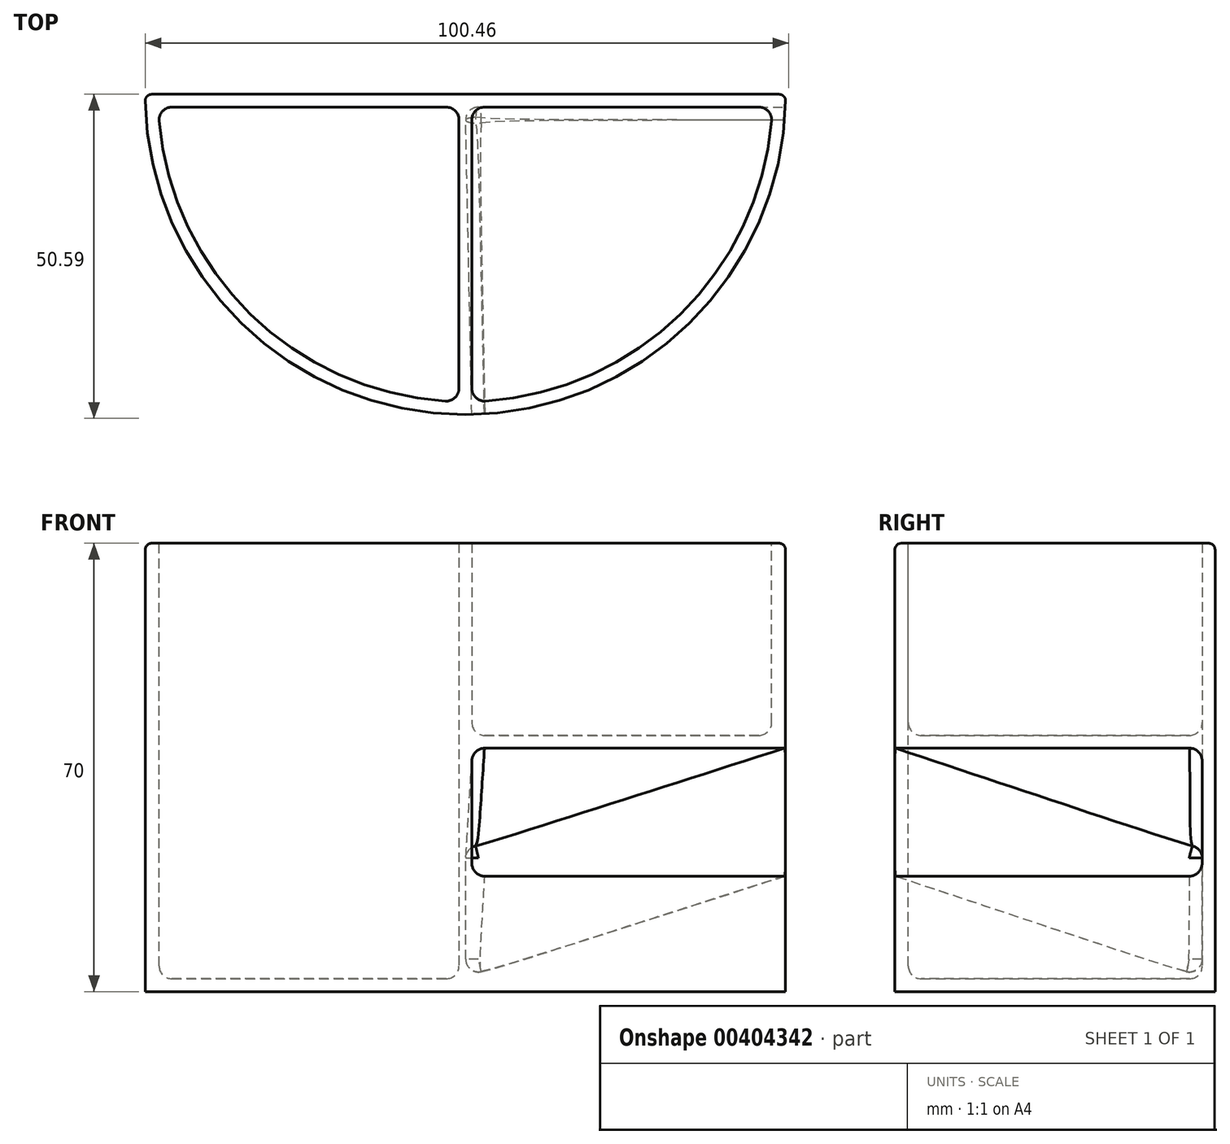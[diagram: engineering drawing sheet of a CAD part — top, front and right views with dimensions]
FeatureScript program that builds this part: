
annotation { "Feature Type Name" : "Feature", "Feature Type Description" : "" }
export const myFeature = defineFeature(function(context is Context, id is Id, definition is map)
    precondition{}
    {
        {
            var Q0;
            Q0=qCreatedBy(makeId("Top.planeOp"),FACE);
            var sketch = newSketch(context, id + "F0", { "sketchPlane" : qUnion([Q0])});
            skArc(sketch, "E0", {"start": v(-50, 0) * mm, "mid": v(0, -50) * mm, "end": v(50, 0) * mm});
            skLineSegment(sketch, "E1", {"start": v(-50, 0) * mm, "end": v(50, 0) * mm});
            skSolve(sketch);
        }
        {
            var Q0;
            Q0 = qSketchRegion(id + "F0", true);
            extrude(context, id + "F1", {"entities" : qUnion([Q0]), "depth" : 70 * mm});
        }
        {
            var Q0;
            Q0=makeQuery(id+"F1.opExtrude","CAP_FACE",FACE,{"disambiguationData":[OSD([sQuery(id+"F0.wireOp",EDGE,"E0"),sQuery(id+"F0.wireOp",EDGE,"E1")])],"isStart":false});
            cPlane(context, id + "F2", {"entities" : qUnion([Q0]), "cplaneType" : CPlaneType.OFFSET, "offset" : 32 * mm, "oppositeDirection" : true, "width" : 150 * mm, "height" : 150 * mm});
        }
        {
            var Q0;
            Q0=qCreatedBy(id+"F2.planeOp",FACE);
            cPlane(context, id + "F3", {"entities" : qUnion([Q0]), "cplaneType" : CPlaneType.OFFSET, "offset" : 20 * mm, "oppositeDirection" : true, "width" : 150 * mm, "height" : 150 * mm});
        }
        {
            var Q0;
            Q0=qCreatedBy(id+"F2.planeOp",FACE);
            var sketch = newSketch(context, id + "F4", { "sketchPlane" : qUnion([Q0])});
            skArc(sketch, "E2", {"start": v(1, -49.99) * mm, "mid": v(35, -35.7) * mm, "end": v(49.96, -2) * mm});
            skSolve(sketch);
        }
        {
            var Q0;
            Q0=qCreatedBy(id+"F3.planeOp",FACE);
            var sketch = newSketch(context, id + "F5", { "sketchPlane" : qUnion([Q0])});
            skArc(sketch, "E3", {"start": v(1, -49.99) * mm, "mid": v(35, -35.7) * mm, "end": v(49.96, -2) * mm});
            skSolve(sketch);
        }
        {
            var Q0;
            Q0=qCreatedBy(makeId("Front.planeOp"),FACE);
            cPlane(context, id + "F6", {"entities" : qUnion([Q0]), "cplaneType" : CPlaneType.OFFSET, "offset" : 2 * mm, "width" : 150 * mm, "height" : 150 * mm});
        }
        {
            var Q0;
            Q0=qCreatedBy(id+"F6.planeOp",FACE);
            var sketch = newSketch(context, id + "F7", { "sketchPlane" : qUnion([Q0])});
            skLineSegment(sketch, "E4", {"start": v(0, 2) * mm, "end": v(0, 22) * mm});
            skSolve(sketch);
        }
        {
            var Q0;
            Q0=sQuery(id+"F7.wireOp",VERTEX,"E4.end");
            var Q1;
            Q1=sQuery(id+"F4.wireOp",EDGE,"E2");
            var Q2;
            Q2=sQuery(id+"F7.wireOp",VERTEX,"E4.end");
            loft(context, id + "F8", {"bodyType" : ToolBodyType.SURFACE, "sheetProfilesArray" : [{ "sheetProfileEntities" : qUnion([Q0]) }], "wireProfilesArray" : [{ "wireProfileEntities" : qUnion([Q1]) }, { "wireProfileEntities" : qUnion([Q2]) }]});
        }
        {
            var Q0;
            Q0=sQuery(id+"F5.wireOp",EDGE,"E3");
            var Q1;
            Q1=sQuery(id+"F7.wireOp",VERTEX,"E4.start");
            loft(context, id + "F9", {"bodyType" : ToolBodyType.SURFACE, "wireProfilesArray" : [{ "wireProfileEntities" : qUnion([Q0]) }, { "wireProfileEntities" : qUnion([Q1]) }]});
        }
        {
            var Q1;
            Q1=makeQuery(id+"F8.opLoft","SWEPT_FACE",FACE,{"disambiguationData":[OSD([sQuery(id+"F4.wireOp",VERTEX,"E2.start"),sQuery(id+"F4.wireOp",VERTEX,"E2.end"),sQuery(id+"F4.wireOp",EDGE,"E2")])]});
            var Q2;
            Q2=makeQuery(id+"F9.opLoft","SWEPT_FACE",FACE,{"disambiguationData":[OSD([sQuery(id+"F5.wireOp",VERTEX,"E3.start"),sQuery(id+"F5.wireOp",VERTEX,"E3.end"),sQuery(id+"F5.wireOp",EDGE,"E3")])]});
            loft(context, id + "F10", {"operationType" : NewBodyOperationType.REMOVE, "sheetProfilesArray" : [{ "sheetProfileEntities" : qUnion([Q1]) }, { "sheetProfileEntities" : qUnion([Q2]) }]});
        }
        {
            var Q0;
            Q0=makeQuery(id+"F1.opExtrude","CAP_FACE",FACE,{"disambiguationData":[OSD([sQuery(id+"F0.wireOp",EDGE,"E0"),sQuery(id+"F0.wireOp",EDGE,"E1")])],"isStart":false});
            var sketch = newSketch(context, id + "F11", { "sketchPlane" : qUnion([Q0])});
            skArc(sketch, "E5", {"start": v(47.96, -2) * mm, "mid": v(33.59, -34.3) * mm, "end": v(1, -47.99) * mm});
            skLineSegment(sketch, "E6", {"start": v(47.96, -2) * mm, "end": v(1, -2) * mm});
            skLineSegment(sketch, "E7", {"start": v(1, -2) * mm, "end": v(1, -47.99) * mm});
            skSolve(sketch);
        }
        {
            var Q0;
            Q0=makeQuery(id+"F11.imprint","IMPRINT",FACE,{"disambiguationData":[TD([[makeQuery(id+"F11.imprint","IMPRINT",EDGE,{"derivedFrom":sQuery(id+"F11.wireOp",EDGE,"E5")}),1.0]])]});
            var sketch = newSketch(context, id + "F12", { "sketchPlane" : qUnion([Q0])});
            skArc(sketch, "E8", {"start": v(-47.96, -2) * mm, "mid": v(-33.59, -34.3) * mm, "end": v(-1, -47.99) * mm});
            skLineSegment(sketch, "E9", {"start": v(-1, -47.99) * mm, "end": v(-1, -2) * mm});
            skLineSegment(sketch, "E10", {"start": v(-1, -2) * mm, "end": v(-47.96, -2) * mm});
            skSolve(sketch);
        }
        {
            var Q0;
            Q0 = qSketchRegion(id + "F11", true);
            extrude(context, id + "F13", {"entities" : qUnion([Q0]), "operationType" : NewBodyOperationType.REMOVE, "oppositeDirection" : true, "depth" : 30 * mm});
        }
        {
            var Q0;
            Q0 = qSketchRegion(id + "F12", true);
            extrude(context, id + "F14", {"entities" : qUnion([Q0]), "operationType" : NewBodyOperationType.REMOVE, "oppositeDirection" : true, "depth" : 68 * mm});
        }
        {
            var Q0;
            Q0=makeQuery(id+"F14.boolean.opBoolean","COPY",EDGE,{"derivedFrom":makeQuery(id+"F14.opExtrude","CAP_EDGE",EDGE,{"disambiguationData":[OSD([sQuery(id+"F12.wireOp",EDGE,"E10")])],"isStart":false})});
            var Q1;
            Q1=makeQuery(id+"F14.boolean.opBoolean","COPY",EDGE,{"derivedFrom":makeQuery(id+"F14.opExtrude","CAP_EDGE",EDGE,{"disambiguationData":[OSD([sQuery(id+"F12.wireOp",EDGE,"E9")])],"isStart":false})});
            var Q2;
            Q2=makeQuery(id+"F14.boolean.opBoolean","COPY",EDGE,{"derivedFrom":makeQuery(id+"F14.opExtrude","SWEPT_EDGE",EDGE,{"disambiguationData":[OSD([sQuery(id+"F12.wireOp",EDGE,"E9"),sQuery(id+"F12.wireOp",EDGE,"E10")])]})});
            var Q3;
            Q3=makeQuery(id+"F14.boolean.opBoolean","COPY",EDGE,{"derivedFrom":makeQuery(id+"F14.opExtrude","SWEPT_EDGE",EDGE,{"disambiguationData":[OSD([sQuery(id+"F12.wireOp",EDGE,"E8"),sQuery(id+"F12.wireOp",EDGE,"E9")])]})});
            var Q4;
            Q4=makeQuery(id+"F14.boolean.opBoolean","COPY",EDGE,{"derivedFrom":makeQuery(id+"F14.opExtrude","CAP_EDGE",EDGE,{"disambiguationData":[OSD([sQuery(id+"F12.wireOp",EDGE,"E8")])],"isStart":false})});
            var Q5;
            Q5=makeQuery(id+"F14.boolean.opBoolean","COPY",EDGE,{"derivedFrom":makeQuery(id+"F14.opExtrude","SWEPT_EDGE",EDGE,{"disambiguationData":[OSD([sQuery(id+"F12.wireOp",EDGE,"E8"),sQuery(id+"F12.wireOp",EDGE,"E10")])]})});
            var Q6;
            Q6=makeQuery(id+"F13.boolean.opBoolean","COPY",EDGE,{"derivedFrom":makeQuery(id+"F13.opExtrude","SWEPT_EDGE",EDGE,{"disambiguationData":[OSD([sQuery(id+"F11.wireOp",EDGE,"E6"),sQuery(id+"F11.wireOp",EDGE,"E7")])]})});
            var Q7;
            Q7=makeQuery(id+"F13.boolean.opBoolean","COPY",EDGE,{"derivedFrom":makeQuery(id+"F13.opExtrude","SWEPT_EDGE",EDGE,{"disambiguationData":[OSD([sQuery(id+"F11.wireOp",EDGE,"E5"),sQuery(id+"F11.wireOp",EDGE,"E6")])]})});
            var Q8;
            Q8=makeQuery(id+"F13.boolean.opBoolean","COPY",EDGE,{"derivedFrom":makeQuery(id+"F13.opExtrude","CAP_EDGE",EDGE,{"disambiguationData":[OSD([sQuery(id+"F11.wireOp",EDGE,"E5")])],"isStart":false})});
            var Q9;
            Q9=makeQuery(id+"F13.boolean.opBoolean","COPY",EDGE,{"derivedFrom":makeQuery(id+"F13.opExtrude","CAP_EDGE",EDGE,{"disambiguationData":[OSD([sQuery(id+"F11.wireOp",EDGE,"E6")])],"isStart":false})});
            var Q10;
            Q10=makeQuery(id+"F13.boolean.opBoolean","COPY",EDGE,{"derivedFrom":makeQuery(id+"F13.opExtrude","CAP_EDGE",EDGE,{"disambiguationData":[OSD([sQuery(id+"F11.wireOp",EDGE,"E7")])],"isStart":false})});
            var Q11;
            Q11=makeQuery(id+"F13.boolean.opBoolean","COPY",EDGE,{"derivedFrom":makeQuery(id+"F13.opExtrude","SWEPT_EDGE",EDGE,{"disambiguationData":[OSD([sQuery(id+"F11.wireOp",EDGE,"E5"),sQuery(id+"F11.wireOp",EDGE,"E7")])]})});
            var Q12;
            Q12=makeQuery(id+"F10.boolean.opBoolean","COPY",EDGE,{"derivedFrom":makeQuery(id+"F10.opLoft","MID_CAP_EDGE",EDGE,{"disambiguationData":[OSD([sQuery(id+"F4.wireOp",VERTEX,"E2.end"),sQuery(id+"F7.wireOp",VERTEX,"E4.end")])],"capPos":0.0})});
            var Q13;
            Q13=makeQuery(id+"F10.boolean.opBoolean","COPY",EDGE,{"derivedFrom":makeQuery(id+"F10.opLoft","MID_CAP_EDGE",EDGE,{"disambiguationData":[OSD([sQuery(id+"F4.wireOp",VERTEX,"E2.start"),sQuery(id+"F4.wireOp",VERTEX,"E2.end"),sQuery(id+"F7.wireOp",VERTEX,"E4.end")])],"capPos":0.0})});
            var Q14;
            Q14=makeQuery(id+"F10.boolean.opBoolean","COPY",EDGE,{"derivedFrom":makeQuery(id+"F10.opLoft","SWEPT_EDGE",EDGE,{"disambiguationData":[OSD([sQuery(id+"F4.wireOp",VERTEX,"E2.end"),sQuery(id+"F5.wireOp",VERTEX,"E3.end"),sQuery(id+"F7.wireOp",VERTEX,"E4.start"),sQuery(id+"F7.wireOp",VERTEX,"E4.end")])]})});
            var Q15;
            Q15=makeQuery(id+"F10.boolean.opBoolean","COPY",EDGE,{"derivedFrom":makeQuery(id+"F10.opLoft","MID_CAP_EDGE",EDGE,{"disambiguationData":[OSD([sQuery(id+"F5.wireOp",VERTEX,"E3.end"),sQuery(id+"F7.wireOp",VERTEX,"E4.start")])],"capPos":1.0})});
            var Q16;
            Q16=makeQuery(id+"F10.boolean.opBoolean","COPY",EDGE,{"derivedFrom":makeQuery(id+"F10.opLoft","MID_CAP_EDGE",EDGE,{"disambiguationData":[OSD([sQuery(id+"F5.wireOp",VERTEX,"E3.start"),sQuery(id+"F5.wireOp",VERTEX,"E3.end"),sQuery(id+"F7.wireOp",VERTEX,"E4.start")])],"capPos":1.0})});
            fillet(context, id + "F15", {"entities" : qUnion([Q0, Q1, Q2, Q3, Q4, Q5, Q6, Q7, Q8, Q9, Q10, Q11, Q12, Q13, Q14, Q15, Q16]), "radius" : 2 * mm, "tangentPropagation" : true, "allowEdgeOverflow" : false});
        }
        {
            var Q0;
            Q0=makeQuery(id+"F10.boolean.opBoolean","COPY",EDGE,{"derivedFrom":makeQuery(id+"F10.opLoft","MID_CAP_EDGE",EDGE,{"disambiguationData":[OSD([sQuery(id+"F5.wireOp",VERTEX,"E3.start"),sQuery(id+"F5.wireOp",VERTEX,"E3.end"),sQuery(id+"F5.wireOp",EDGE,"E3")])],"capPos":1.0})});
            var Q1;
            {var subQ0=sQuery(id+"F0.wireOp",EDGE,"E1");var subQ1=sQuery(id+"F0.wireOp",EDGE,"E0");Q1=makeQuery(id+"F1.opExtrude","SWEPT_EDGE",EDGE,{"disambiguationData":[OSD([subQ1,subQ0]),TDD([makeQuery(id+"F0.imprint","INTERSECT",VERTEX,{"disambiguationData":[OD(1.0)],"derivedFrom":[subQ1,subQ0]})])]});}
            var Q2;
            Q2=makeQuery(id+"F1.opExtrude","CAP_EDGE",EDGE,{"disambiguationData":[OSD([sQuery(id+"F0.wireOp",EDGE,"E1")])],"isStart":false});
            var Q3;
            Q3=makeQuery(id+"F1.opExtrude","CAP_EDGE",EDGE,{"disambiguationData":[OSD([sQuery(id+"F0.wireOp",EDGE,"E0")])],"isStart":false});
            var Q4;
            {var subQ0=sQuery(id+"F0.wireOp",EDGE,"E1");var subQ1=sQuery(id+"F0.wireOp",EDGE,"E0");Q4=makeQuery(id+"F1.opExtrude","SWEPT_EDGE",EDGE,{"disambiguationData":[OSD([subQ1,subQ0]),TDD([makeQuery(id+"F0.imprint","INTERSECT",VERTEX,{"disambiguationData":[OD(0.0)],"derivedFrom":[subQ1,subQ0]})])]});}
            var Q5;
            Q5=makeQuery(id+"F13.boolean.opBoolean","COPY",EDGE,{"derivedFrom":makeQuery(id+"F13.opExtrude","CAP_EDGE",EDGE,{"disambiguationData":[OSD([sQuery(id+"F11.wireOp",EDGE,"E7")])],"isStart":true})});
            var Q6;
            Q6=makeQuery(id+"F14.boolean.opBoolean","COPY",EDGE,{"derivedFrom":makeQuery(id+"F14.opExtrude","CAP_EDGE",EDGE,{"disambiguationData":[OSD([sQuery(id+"F12.wireOp",EDGE,"E9")])],"isStart":true})});
            fillet(context, id + "F16", {"entities" : qUnion([Q0, Q1, Q2, Q3, Q4, Q5, Q6]), "radius" : 1 * mm, "tangentPropagation" : true, "allowEdgeOverflow" : false});
        }
    });
